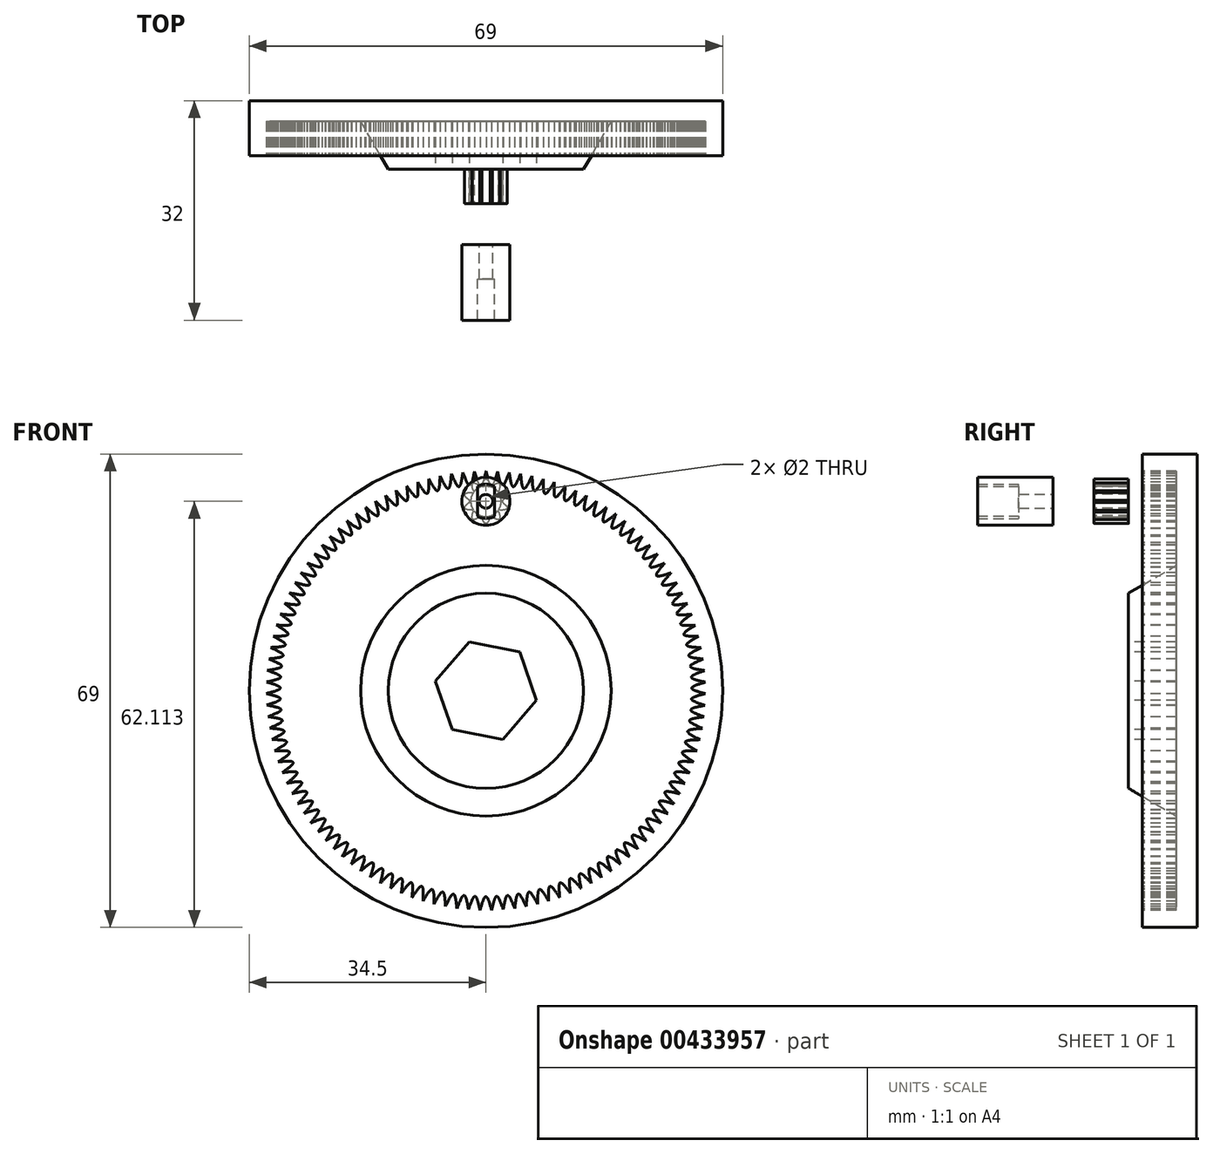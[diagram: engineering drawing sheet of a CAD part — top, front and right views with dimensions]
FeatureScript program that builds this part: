
annotation { "Feature Type Name" : "Feature", "Feature Type Description" : "" }
export const myFeature = defineFeature(function(context is Context, id is Id, definition is map)
    precondition{}
    {
        {
            var Q0;
            Q0=qCreatedBy(makeId("Front.planeOp"),FACE);
            var sketch = newSketch(context, id + "F0", { "sketchPlane" : qUnion([Q0])});
            skCircle(sketch, "E0", {"center": v(0, 0) * mm, "radius": 34.5 * mm});
            skSolve(sketch);
        }
        {
            var Q0;
            Q0=makeQuery(id+"F0.imprint","IMPRINT",FACE,{"disambiguationData":[TD([[makeQuery(id+"F0.imprint","IMPRINT",EDGE,{"derivedFrom":sQuery(id+"F0.wireOp",EDGE,"E0")}),1.0]])]});
            extrude(context, id + "F1", {"entities" : qUnion([Q0]), "depth" : 3 * mm});
        }
        {
            var Q0;
            Q0=qCreatedBy(makeId("Front.planeOp"),FACE);
            var sketch = newSketch(context, id + "F2", { "sketchPlane" : qUnion([Q0])});
            skCircle(sketch, "E1", {"center": v(0, 0) * mm, "radius": 20 * mm});
            skSolve(sketch);
        }
        {
            var Q0;
            Q0 = qSketchRegion(id + "F2", true);
            extrude(context, id + "F3", {"entities" : qUnion([Q0]), "operationType" : NewBodyOperationType.ADD, "depth" : 10 * mm, "hasDraft" : true, "draftAngle" : 30 * degree, "draftPullDirection" : true});
        }
        {
            var Q0;
            Q0=makeQuery(id+"F3.opExtrude","CAP_FACE",FACE,{"disambiguationData":[OSD([sQuery(id+"F2.wireOp",EDGE,"E1")])],"isStart":false});
            var sketch = newSketch(context, id + "F4", { "sketchPlane" : qUnion([Q0])});
            skCircle(sketch, "E2.cCircle", {"center": v(0, 0) * mm, "radius": 7.5 * mm, "construction": true});
            skLineSegment(sketch, "E2.0", {"start": v(2.46, -7.1) * mm, "end": v(-4.91, -5.67) * mm});
            skLineSegment(sketch, "E2.1", {"start": v(-4.91, -5.67) * mm, "end": v(-7.37, 1.42) * mm});
            skLineSegment(sketch, "E2.2", {"start": v(-7.37, 1.42) * mm, "end": v(-2.46, 7.1) * mm});
            skLineSegment(sketch, "E2.3", {"start": v(-2.46, 7.1) * mm, "end": v(4.91, 5.67) * mm});
            skLineSegment(sketch, "E2.4", {"start": v(4.91, 5.67) * mm, "end": v(7.37, -1.42) * mm});
            skLineSegment(sketch, "E2.5", {"start": v(7.37, -1.42) * mm, "end": v(2.46, -7.1) * mm});
            skSolve(sketch);
        }
        {
            var Q0;
            Q0 = qSketchRegion(id + "F4", true);
            extrude(context, id + "F5", {"entities" : qUnion([Q0]), "operationType" : NewBodyOperationType.ADD, "oppositeDirection" : true, "depth" : 7 * mm});
        }
        {
            var Q0;
            Q0=makeQuery(id+"F4.imprint","IMPRINT",FACE,{"disambiguationData":[TD([[makeQuery(id+"F4.imprint","IMPRINT",EDGE,{"derivedFrom":sQuery(id+"F4.wireOp",EDGE,"E2.0")}),-1.0]])]});
            extrude(context, id + "F6", {"entities" : qUnion([Q0]), "operationType" : NewBodyOperationType.REMOVE, "oppositeDirection" : true, "depth" : 7 * mm});
        }
        {
            var Q0;
            Q0=makeQuery(id+"F1.opExtrude","CAP_FACE",FACE,{"disambiguationData":[OSD([sQuery(id+"F0.wireOp",EDGE,"E0")])],"isStart":false});
            var sketch = newSketch(context, id + "F7", { "sketchPlane" : qUnion([Q0])});
            skCircle(sketch, "E3", {"center": v(0, 0) * mm, "radius": 34.5 * mm});
            skSolve(sketch);
        }
        {
            var Q0;
            Q0=makeQuery(id+"F7.imprint","IMPRINT",FACE,{"disambiguationData":[TD([[makeQuery(id+"F7.imprint","IMPRINT",EDGE,{"derivedFrom":sQuery(id+"F7.wireOp",EDGE,"E3")}),1.0]])]});
            var sketch = newSketch(context, id + "F8", { "sketchPlane" : qUnion([Q0])});
            skCircle(sketch, "E4", {"center": v(0, 0) * mm, "radius": 30 * mm});
            skSolve(sketch);
        }
        {
            var Q0;
            Q0=makeQuery(id+"F8.imprint","IMPRINT",FACE,{"disambiguationData":[TD([[makeQuery(id+"F8.imprint","IMPRINT",EDGE,{"derivedFrom":sQuery(id+"F8.wireOp",EDGE,"E4")}),-1.0]])]});
            extrude(context, id + "F9", {"entities" : qUnion([Q0]), "operationType" : NewBodyOperationType.ADD, "depth" : 5 * mm});
        }
        {
            var Q0;
            Q0=makeQuery(id+"F9.opExtrude","CAP_FACE",FACE,{"disambiguationData":[OSD([sQuery(id+"F7.wireOp",EDGE,"E3"),sQuery(id+"F8.wireOp",EDGE,"E4")])],"isStart":false});
            var sketch = newSketch(context, id + "F10", { "sketchPlane" : qUnion([Q0])});
            skCircle(sketch, "E5", {"center": v(0, 0) * mm, "radius": 32 * mm});
            skLineSegment(sketch, "E6", {"start": v(0, 0) * mm, "end": v(0, 48.21) * mm, "construction": true});
            skLineSegment(sketch, "E7", {"start": v(0, 0) * mm, "end": v(-2.58, 49.28) * mm, "construction": true});
            skLineSegment(sketch, "E8", {"start": v(0, 0) * mm, "end": v(-5.16, 49.1) * mm, "construction": true});
            skLineSegment(sketch, "E9", {"start": v(0, 0) * mm, "end": v(-1.3, 49.31) * mm, "construction": true});
            skPoint(sketch, "E9.endSnap0", {"position": v(-1.3, 24.64) * mm});
            skLineSegment(sketch, "E10", {"start": v(0, 0) * mm, "end": v(-3.87, 49.23) * mm, "construction": true});
            skFitSpline(sketch, "E11", {"points": [v(0, 32) * mm, v(-0.79, 29.99) * mm, v(-1.67, 31.96) * mm], "startDerivative": vector(-1.57, -6) * mm, "endDerivative": vector(-1.88, 5.92) * mm});
            skFitSpline(sketch, "E12", {"points": [v(-1.67, 31.96) * mm, v(-2.35, 29.9) * mm, v(-3.34, 31.82) * mm], "startDerivative": vector(-1.25, -6.08) * mm, "endDerivative": vector(-2.2, 5.81) * mm});
            skLineSegment(sketch, "E13", {"start": v(0, 0) * mm, "end": v(2.62, 49.95) * mm, "construction": true});
            skLineSegment(sketch, "E14", {"start": v(0, 0) * mm, "end": v(5.2, 49.51) * mm, "construction": true});
            skLineSegment(sketch, "E15", {"start": v(0, 0) * mm, "end": v(1.3, 49.92) * mm, "construction": true});
            skLineSegment(sketch, "E16", {"start": v(0, 0) * mm, "end": v(3.93, 49.95) * mm, "construction": true});
            skSolve(sketch);
        }
        {
            var Q0;
            {var subQ1=sQuery(id+"F10.wireOp",EDGE,"E11");var subQ3=makeQuery(id+"F9.opExtrude","CAP_EDGE",EDGE,{"disambiguationData":[OSD([sQuery(id+"F8.wireOp",EDGE,"E4")])],"isStart":false});var subQ4=makeQuery(id+"F10.imprint","INTERSECT",VERTEX,{"derivedFrom":[subQ3,subQ1]});Q0=makeQuery(id+"F10.imprint","IMPRINT",FACE,{"disambiguationData":[TD([[makeQuery(id+"F10.imprint","IMPRINT",EDGE,{"disambiguationData":[TD([[subQ4,-1.0]])],"derivedFrom":subQ3}),-1.0]])]});}
            extrude(context, id + "F11", {"entities" : qUnion([Q0]), "operationType" : NewBodyOperationType.REMOVE, "oppositeDirection" : true, "depth" : 5 * mm});
        }
        {
            var Q0;
            Q0=makeQuery(id+"F11.boolean.opBoolean","COPY",FACE,{"derivedFrom":makeQuery(id+"F11.opExtrude","SWEPT_FACE",FACE,{"disambiguationData":[OSD([sQuery(id+"F10.wireOp",EDGE,"E12")])]})});
            var Q1;
            Q1=makeQuery(id+"F11.boolean.opBoolean","COPY",FACE,{"derivedFrom":makeQuery(id+"F11.opExtrude","SWEPT_FACE",FACE,{"disambiguationData":[OSD([sQuery(id+"F10.wireOp",EDGE,"E11")])]})});
            var Q2;
            Q2=makeQuery(id+"F9.opExtrude","SWEPT_FACE",FACE,{"disambiguationData":[OSD([sQuery(id+"F8.wireOp",EDGE,"E4")])]});
            circularPattern(context, id + "F12", {"patternType" : PatternType.FACE, "faces" : qUnion([Q0, Q1]), "axis" : qUnion([Q2]), "angle" : 360 * degree, "instanceCount" : 119, "equalSpace" : true});
        }
        {
            var Q0;
            Q0=qCreatedBy(makeId("Front.planeOp"),FACE);
            cPlane(context, id + "F13", {"entities" : qUnion([Q0]), "cplaneType" : CPlaneType.OFFSET, "offset" : 15 * mm, "width" : 150 * mm, "height" : 150 * mm});
        }
        {
            var Q0;
            Q0=qCreatedBy(id+"F13.planeOp",FACE);
            var sketch = newSketch(context, id + "F14", { "sketchPlane" : qUnion([Q0])});
            skCircle(sketch, "E17", {"center": v(0, 27.61) * mm, "radius": 3.25 * mm});
            skCircle(sketch, "E18", {"center": v(0, 27.61) * mm, "radius": 2.22 * mm});
            skFitSpline(sketch, "E19", {"points": [v(-0.65, 29.74) * mm, v(0, 30.86) * mm, v(0.7, 29.72) * mm], "startDerivative": vector(1.3, 4.4) * mm, "endDerivative": vector(1.4, -4.41) * mm});
            skCircle(sketch, "E20", {"center": v(0, 27.61) * mm, "radius": 1 * mm});
            skFitSpline(sketch, "E21", {"points": [v(-0.58, 29.98) * mm, v(-0.59, 29.76) * mm], "startDerivative": vector(-0.01, -0.22) * mm, "endDerivative": vector(-0.01, -0.22) * mm});
            skFitSpline(sketch, "E22", {"points": [v(0.61, 29.97) * mm, v(0.62, 29.75) * mm], "startDerivative": vector(0, -0.23) * mm, "endDerivative": vector(0, -0.23) * mm});
            skFitSpline(sketch, "E23", {"points": [v(-0.59, 29.76) * mm, v(0, 29.84) * mm, v(0.62, 29.75) * mm], "startDerivative": vector(1.19, 0.24) * mm, "endDerivative": vector(1.24, -0.26) * mm});
            skSolve(sketch);
        }
        {
            var Q0;
            Q0=makeQuery(id+"F14.imprint","IMPRINT",FACE,{"disambiguationData":[TD([[makeQuery(id+"F14.imprint","IMPRINT",EDGE,{"derivedFrom":sQuery(id+"F14.wireOp",EDGE,"E20")}),-1.0]])]});
            var Q1;
            {var subQ0=sQuery(id+"F14.wireOp",EDGE,"E21");Q1=makeQuery(id+"F14.imprint","IMPRINT",FACE,{"disambiguationData":[TD([[makeQuery(id+"F14.imprint","IMPRINT",EDGE,{"derivedFrom":subQ0}),1.0]])]});}
            extrude(context, id + "F15", {"entities" : qUnion([Q0, Q1]), "oppositeDirection" : true, "depth" : 5 * mm});
        }
        {
            var Q0;
            Q0=makeQuery(id+"F15.opExtrude","SWEPT_BODY",BODY,{"disambiguationData":[OSD([sQuery(id+"F14.wireOp",EDGE,"E18"),sQuery(id+"F14.wireOp",EDGE,"E19"),sQuery(id+"F14.wireOp",EDGE,"E20"),sQuery(id+"F14.wireOp",EDGE,"E21"),sQuery(id+"F14.wireOp",EDGE,"E22")])]});
            var Q1;
            Q1=sQuery(id+"F14.wireOp",EDGE,"E18");
            circularPattern(context, id + "F16", {"entities" : qUnion([Q0]), "axis" : qUnion([Q1]), "angle" : 360 * degree, "instanceCount" : 10, "equalSpace" : true});
        }
        {
            var Q0;
            Q0=qCreatedBy(id+"F13.planeOp",FACE);
            cPlane(context, id + "F17", {"entities" : qUnion([Q0]), "cplaneType" : CPlaneType.OFFSET, "offset" : 5 * mm, "width" : 150 * mm, "height" : 150 * mm});
        }
        {
            var Q0;
            Q0=qCreatedBy(id+"F17.planeOp",FACE);
            var sketch = newSketch(context, id + "F18", { "sketchPlane" : qUnion([Q0])});
            skCircle(sketch, "E24", {"center": v(0, 27.61) * mm, "radius": 1 * mm});
            skCircle(sketch, "E25", {"center": v(0, 27.61) * mm, "radius": 3.5 * mm});
            skSolve(sketch);
        }
        {
            var Q0;
            Q0=makeQuery(id+"F18.imprint","IMPRINT",FACE,{"disambiguationData":[TD([[makeQuery(id+"F18.imprint","IMPRINT",EDGE,{"derivedFrom":sQuery(id+"F18.wireOp",EDGE,"E24")}),-1.0]])]});
            extrude(context, id + "F19", {"entities" : qUnion([Q0]), "depth" : 6 * mm, "hasSecondDirection" : true, "secondDirectionOppositeDirection" : false, "secondDirectionDepth" : 1 * mm});
        }
        {
            var Q0;
            Q0=makeQuery(id+"F19.opExtrude","CAP_FACE",FACE,{"disambiguationData":[OSD([sQuery(id+"F18.wireOp",EDGE,"E24"),sQuery(id+"F18.wireOp",EDGE,"E25")])],"isStart":false});
            var sketch = newSketch(context, id + "F20", { "sketchPlane" : qUnion([Q0])});
            skCircle(sketch, "E26", {"center": v(0, 27.61) * mm, "radius": 3.5 * mm});
            skCircle(sketch, "E27", {"center": v(0, 27.61) * mm, "radius": 2.5 * mm});
            skLineSegment(sketch, "E28", {"start": v(-1.25, 29.78) * mm, "end": v(-1.25, 25.45) * mm});
            skLineSegment(sketch, "E29", {"start": v(1.25, 29.78) * mm, "end": v(1.25, 25.45) * mm});
            skSolve(sketch);
        }
        {
            var Q0;
            Q0=makeQuery(id+"F20.imprint","IMPRINT",FACE,{"disambiguationData":[TD([[makeQuery(id+"F20.imprint","IMPRINT",EDGE,{"derivedFrom":sQuery(id+"F20.wireOp",EDGE,"E26")}),1.0]])]});
            var Q1;
            {var subQ0=sQuery(id+"F20.wireOp",EDGE,"E28");var subQ1=sQuery(id+"F20.wireOp",EDGE,"E27");var subQ2=makeQuery(id+"F20.imprint","INTERSECT",VERTEX,{"disambiguationData":[OD(0.0)],"derivedFrom":[subQ1,subQ0]});Q1=makeQuery(id+"F20.imprint","IMPRINT",FACE,{"disambiguationData":[TD([[makeQuery(id+"F20.imprint","IMPRINT",EDGE,{"disambiguationData":[TD([[subQ2,-1.0]])],"derivedFrom":subQ1}),1.0]])]});}
            var Q2;
            {var subQ0=sQuery(id+"F20.wireOp",EDGE,"E28");var subQ1=makeQuery(id+"F19.opExtrude","CAP_EDGE",EDGE,{"disambiguationData":[OSD([sQuery(id+"F18.wireOp",EDGE,"E25")])],"isStart":false});var subQ2=makeQuery(id+"F20.imprint","INTERSECT",VERTEX,{"disambiguationData":[OD(0.0)],"derivedFrom":[subQ1,subQ0]});Q2=makeQuery(id+"F20.imprint","IMPRINT",FACE,{"disambiguationData":[TD([[makeQuery(id+"F20.imprint","IMPRINT",EDGE,{"disambiguationData":[TD([[subQ2,-1.0]])],"derivedFrom":subQ0}),-1.0]])]});}
            var Q3;
            {var subQ0=sQuery(id+"F20.wireOp",EDGE,"E29");var subQ1=sQuery(id+"F20.wireOp",EDGE,"E27");var subQ2=makeQuery(id+"F20.imprint","INTERSECT",VERTEX,{"disambiguationData":[OD(0.0)],"derivedFrom":[subQ1,subQ0]});Q3=makeQuery(id+"F20.imprint","IMPRINT",FACE,{"disambiguationData":[TD([[makeQuery(id+"F20.imprint","IMPRINT",EDGE,{"disambiguationData":[TD([[subQ2,1.0]])],"derivedFrom":subQ1}),1.0]])]});}
            var Q4;
            {var subQ0=sQuery(id+"F20.wireOp",EDGE,"E29");var subQ1=makeQuery(id+"F19.opExtrude","CAP_EDGE",EDGE,{"disambiguationData":[OSD([sQuery(id+"F18.wireOp",EDGE,"E25")])],"isStart":false});var subQ2=makeQuery(id+"F20.imprint","INTERSECT",VERTEX,{"disambiguationData":[OD(0.0)],"derivedFrom":[subQ1,subQ0]});Q4=makeQuery(id+"F20.imprint","IMPRINT",FACE,{"disambiguationData":[TD([[makeQuery(id+"F20.imprint","IMPRINT",EDGE,{"disambiguationData":[TD([[subQ2,-1.0]])],"derivedFrom":subQ0}),1.0]])]});}
            extrude(context, id + "F21", {"entities" : qUnion([Q0, Q1, Q2, Q3, Q4]), "operationType" : NewBodyOperationType.ADD, "depth" : 6 * mm});
        }
    });
